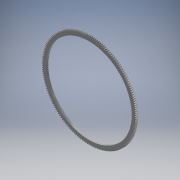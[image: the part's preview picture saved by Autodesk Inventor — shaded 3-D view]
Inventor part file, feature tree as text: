
AUTODESK INVENTOR PART (.ipt)
format: ipt  version: 2017 (Build 210142000, 142)  size: 863,232 bytes
history: native  units: mm (DEFAULTED — no unit token found)
features: plane x3, other x3, sketch x3, extrude x2
ambient origin geometry x8: Origin, YZ Plane, XZ Plane, XY Plane, X Axis, Y Axis, Z Axis, Center Point
bodies: Solid1 (feature_tree)
feature tree (11):
  extrude  "Extrusion1"  Depth=6.35mm TaperAngle=0.0deg
  plane  "Work Plane1"
  plane  "Work Plane2"
  plane  "Work Plane3"
  other  "Spur Gear"
  extrude  "Extrusion2"  Depth=76.2mm TaperAngle=0.0deg
  sketch  "Sketch1"  dims[d0=301.413333mm d1=6.35mm d2=0.0mm]
  sketch  "Sketch2"  dims[d3=298.026667mm d4=76.2mm d5=0.0mm]
  other  "Srf1"
  sketch  "Sketch3"  dims[d6=0.0mm d7=0.1785mm d9=0.0mm d14=0.0mm d15=161.713333mm d16=0.0mm d17=0.0mm d18=0.0mm d19=161.713333mm d20=272.771792mm d21=25.4mm d22=0.0mm]
  other  "Pitch Diameter"
